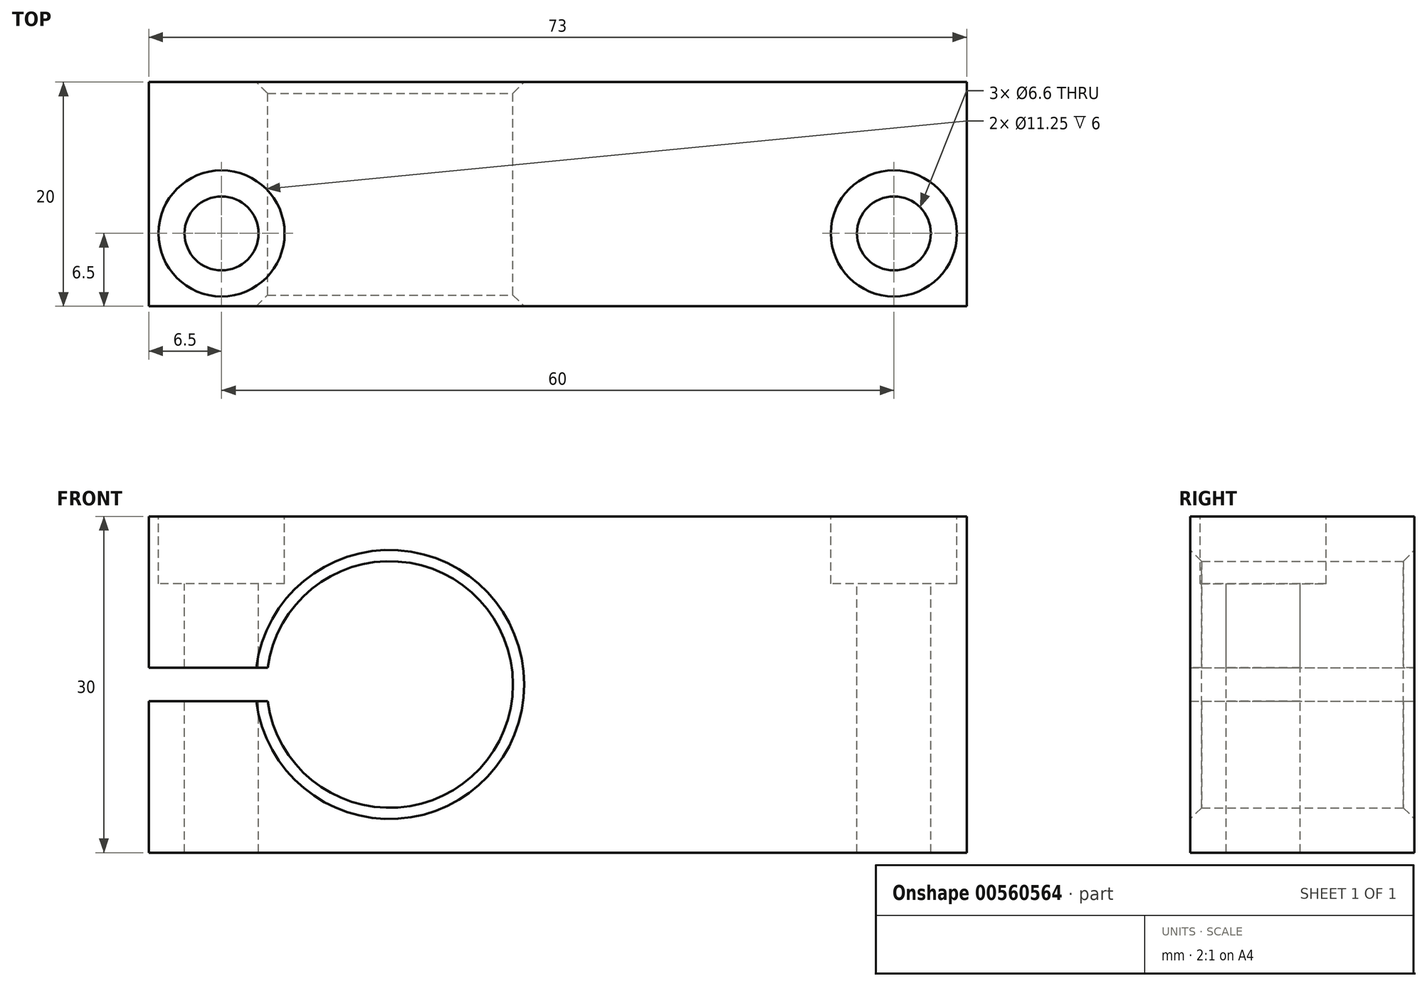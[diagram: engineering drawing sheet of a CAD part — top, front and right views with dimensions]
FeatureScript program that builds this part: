
annotation { "Feature Type Name" : "Feature", "Feature Type Description" : "" }
export const myFeature = defineFeature(function(context is Context, id is Id, definition is map)
    precondition{}
    {
        {
            var Q0;
            Q0=qCreatedBy(makeId("Front.planeOp"),FACE);
            var sketch = newSketch(context, id + "F0", { "sketchPlane" : qUnion([Q0])});
            skLineSegment(sketch, "E0.bottom", {"start": v(-36.5, 15) * mm, "end": v(36.5, 15) * mm});
            skLineSegment(sketch, "E0.top", {"start": v(-36.5, -15) * mm, "end": v(36.5, -15) * mm});
            skLineSegment(sketch, "E0.left", {"start": v(-36.5, 15) * mm, "end": v(-36.5, -15) * mm});
            skLineSegment(sketch, "E0.right", {"start": v(36.5, 15) * mm, "end": v(36.5, -15) * mm});
            skPoint(sketch, "E0.middle", {"position": v(0, 0) * mm});
            skLineSegment(sketch, "E1", {"start": v(-26, 15) * mm, "end": v(-26, -15) * mm, "construction": true});
            skLineSegment(sketch, "E2", {"start": v(0, 15) * mm, "end": v(0, -15) * mm, "construction": true});
            skLineSegment(sketch, "E3.MirrorCS", {"start": v(26, 15) * mm, "end": v(26, -15) * mm, "construction": true});
            skCircle(sketch, "E4", {"center": v(-15, 0) * mm, "radius": 11 * mm});
            skLineSegment(sketch, "E5.bottom", {"start": v(-36.5, 1.5) * mm, "end": v(-15.5, 1.5) * mm});
            skLineSegment(sketch, "E5.top", {"start": v(-36.5, -1.5) * mm, "end": v(-15.5, -1.5) * mm});
            skLineSegment(sketch, "E5.left", {"start": v(-36.5, 1.5) * mm, "end": v(-36.5, -1.5) * mm});
            skLineSegment(sketch, "E5.right", {"start": v(-15.5, 1.5) * mm, "end": v(-15.5, -1.5) * mm});
            skPoint(sketch, "E5.middle", {"position": v(-26, 0) * mm});
            skSolve(sketch);
        }
        {
            var Q0;
            {var subQ5=sQuery(id+"F0.wireOp",EDGE,"E0.bottom");Q0=makeQuery(id+"F0.imprint","IMPRINT",FACE,{"disambiguationData":[TD([[makeQuery(id+"F0.imprint","IMPRINT",EDGE,{"derivedFrom":subQ5}),-1.0]])]});}
            extrude(context, id + "F1", {"entities" : qUnion([Q0]), "depth" : 20 * mm, "offsetDistance" : 25 * mm});
        }
        {
            var Q0;
            Q0=makeQuery(id+"F1.opExtrude","SWEPT_FACE",FACE,{"disambiguationData":[OSD([sQuery(id+"F0.wireOp",EDGE,"E0.bottom")])]});
            var sketch = newSketch(context, id + "F2", { "sketchPlane" : qUnion([Q0])});
            skPoint(sketch, "E6", {"position": v(-30, -13.5) * mm});
            skLineSegment(sketch, "E7", {"start": v(0, 0) * mm, "end": v(0, -20) * mm, "construction": true});
            skPoint(sketch, "E8.MirrorP", {"position": v(30, -13.5) * mm});
            skSolve(sketch);
        }
        {
            var Q0;
            Q0=sQuery(id+"F2.wireOp",VERTEX,"E6");
            var Q1;
            Q1=sQuery(id+"F2.wireOp",VERTEX,"E8.MirrorP");
            var Q2;
            Q2=makeQuery(id+"F1.opExtrude","SWEPT_BODY",BODY,{"disambiguationData":[OSD([sQuery(id+"F0.wireOp",EDGE,"E0.bottom"),sQuery(id+"F0.wireOp",EDGE,"E0.top"),sQuery(id+"F0.wireOp",EDGE,"E0.left"),sQuery(id+"F0.wireOp",EDGE,"E0.right"),sQuery(id+"F0.wireOp",EDGE,"E4"),sQuery(id+"F0.wireOp",EDGE,"E5.bottom"),sQuery(id+"F0.wireOp",EDGE,"E5.top")])]});
            hole(context, id + "F3", {"style" : HoleStyle.C_BORE, "endStyle" : HoleEndStyle.THROUGH, "standardTappedOrClearance" : lookupTablePath({ "standard" : "ISO", "fit" : "Normal", "size" : "M6", "type" : "Clearance" }), "standardBlindInLast" : lookupTablePath({ "fit" : "Standard", "standard" : "ISO", "size" : "M6", "type" : "Clearance" }), "holeDiameter" : 6.6 * mm, "cBoreDiameter" : 11.25 * mm, "cBoreDepth" : 6 * mm, "isTappedThrough" : true, "tappedDepth" : 12 * mm, "tapClearance" : 3, "locations" : qUnion([Q0, Q1]), "scope" : qUnion([Q2])});
        }
        {
            var Q0;
            Q0=makeQuery(id+"F1.opExtrude","CAP_EDGE",EDGE,{"disambiguationData":[OSD([sQuery(id+"F0.wireOp",EDGE,"E4")])],"isStart":false});
            var Q1;
            Q1=makeQuery(id+"F1.opExtrude","CAP_EDGE",EDGE,{"disambiguationData":[OSD([sQuery(id+"F0.wireOp",EDGE,"E4")])],"isStart":true});
            chamfer(context, id + "F4", {"entities" : qUnion([Q0, Q1]), "width" : 1 * mm, "tangentPropagation" : true});
        }
    });
